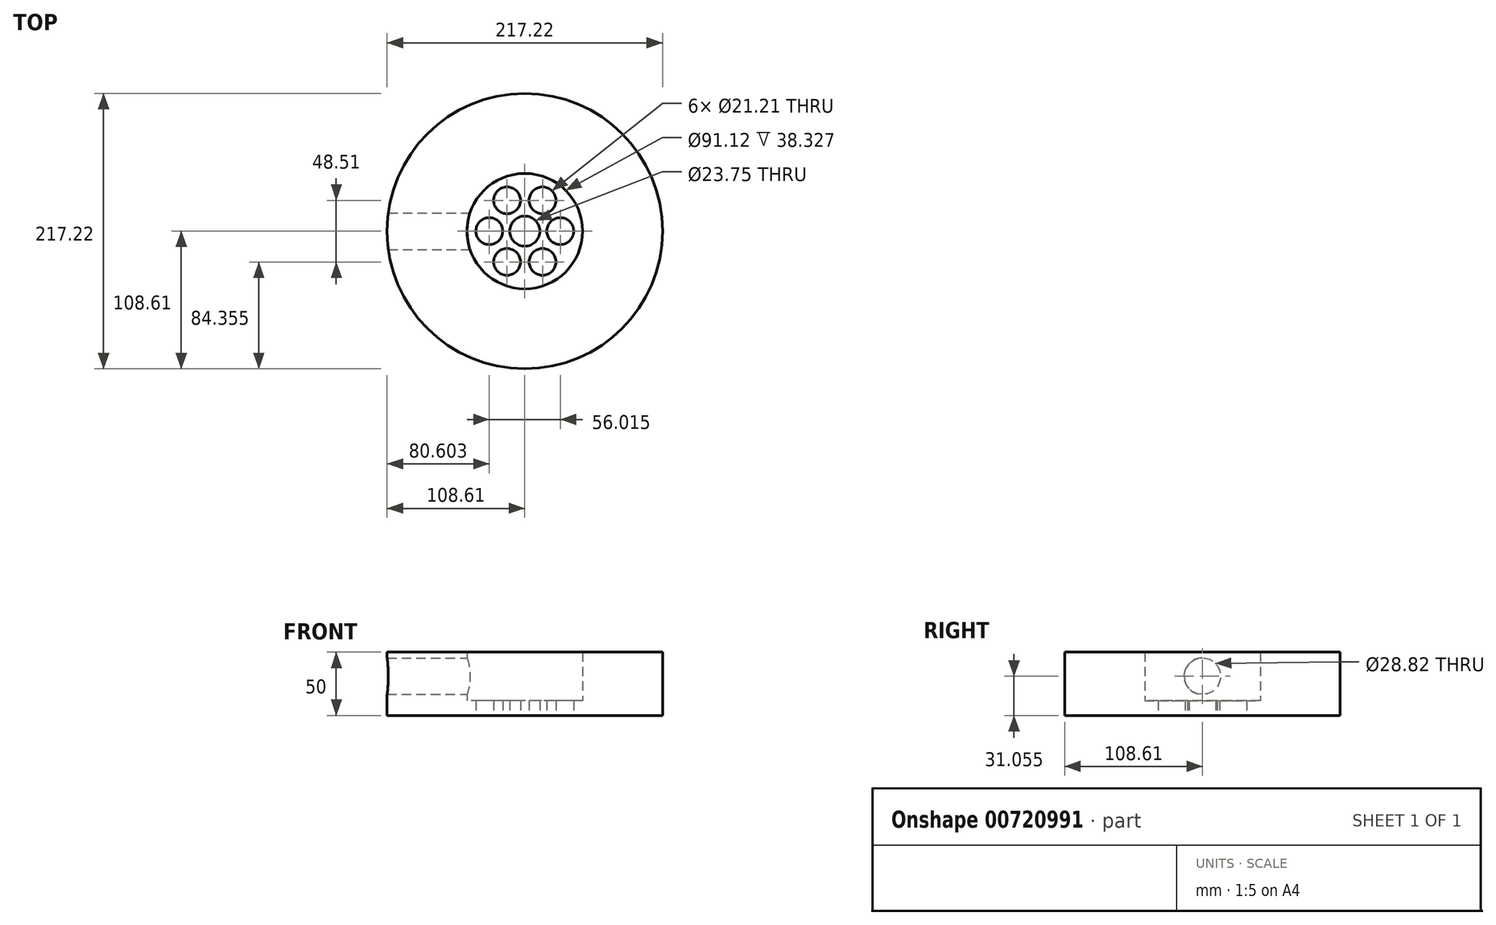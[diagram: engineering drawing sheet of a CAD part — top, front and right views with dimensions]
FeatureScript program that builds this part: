
annotation { "Feature Type Name" : "Feature", "Feature Type Description" : "" }
export const myFeature = defineFeature(function(context is Context, id is Id, definition is map)
    precondition{}
    {
        {
            var Q0;
            Q0=qCreatedBy(makeId("Top.planeOp"),FACE);
            var sketch = newSketch(context, id + "F0", { "sketchPlane" : qUnion([Q0])});
            skCircle(sketch, "E0", {"center": v(0, 0) * mm, "radius": 108.61 * mm});
            skCircle(sketch, "E1", {"center": v(0, 0) * mm, "radius": 45.56 * mm});
            skCircle(sketch, "E2", {"center": v(0, 0) * mm, "radius": 11.88 * mm});
            skCircle(sketch, "E3", {"center": v(-28, 0) * mm, "radius": 10.6 * mm});
            skCircle(sketch, "E4.1.0", {"center": v(-14, -24.25) * mm, "radius": 10.6 * mm});
            skCircle(sketch, "E4.2.0", {"center": v(14, -24.25) * mm, "radius": 10.6 * mm});
            skCircle(sketch, "E4.3.0", {"center": v(28, 0) * mm, "radius": 10.6 * mm});
            skCircle(sketch, "E4.4.0", {"center": v(14, 24.25) * mm, "radius": 10.6 * mm});
            skCircle(sketch, "E4.5.0", {"center": v(-14, 24.25) * mm, "radius": 10.6 * mm});
            skSolve(sketch);
        }
        {
            var Q0;
            Q0 = qSketchRegion(id + "F0", true);
            extrude(context, id + "F1", {"entities" : qUnion([Q0]), "depth" : 50 * mm, "offsetDistance" : 25 * mm});
        }
        {
            var Q0;
            Q0=makeQuery(id+"F0.imprint","IMPRINT",FACE,{"disambiguationData":[TD([[makeQuery(id+"F0.imprint","IMPRINT",EDGE,{"derivedFrom":sQuery(id+"F0.wireOp",EDGE,"E1")}),1.0]])]});
            extrude(context, id + "F2", {"entities" : qUnion([Q0]), "operationType" : NewBodyOperationType.ADD, "depth" : 11.67 * mm, "offsetDistance" : 25 * mm});
        }
        {
            var Q0;
            Q0=qCreatedBy(makeId("Right.planeOp"),FACE);
            var sketch = newSketch(context, id + "F3", { "sketchPlane" : qUnion([Q0])});
            skCircle(sketch, "E5", {"center": v(0, 31.06) * mm, "radius": 14.41 * mm});
            skSolve(sketch);
        }
        {
            var Q0;
            Q0 = qSketchRegion(id + "F3", true);
            var Q1;
            Q1=makeQuery(id+"F1.opExtrude","SWEPT_FACE",FACE,{"disambiguationData":[OSD([sQuery(id+"F0.wireOp",EDGE,"E0")])]});
            extrude(context, id + "F4", {"entities" : qUnion([Q0]), "operationType" : NewBodyOperationType.REMOVE, "endBound" : BoundingType.UP_TO_SURFACE, "oppositeDirection" : true, "depth" : 25 * mm, "endBoundEntityFace" : qUnion([Q1]), "offsetDistance" : 25 * mm});
        }
        {
            var Q0;
            Q0=qCreatedBy(makeId("Front.planeOp"),FACE);
            var sketch = newSketch(context, id + "F5", { "sketchPlane" : qUnion([Q0])});
            skFitSpline(sketch, "E6", {"points": [v(17.4, 11.67) * mm, v(45.56, 45.47) * mm], "startDerivative": vector(-8.12, 73.98) * mm, "endDerivative": vector(61.97, -2.03) * mm});
            skFitSpline(sketch, "E7", {"points": [v(38.61, 11.67) * mm, v(45.56, 16.64) * mm], "startDerivative": vector(0.18, 10.79) * mm, "endDerivative": vector(12.4, -1.23) * mm});
            skFitSpline(sketch, "E8.0", {"points": [v(45.56, 16.64) * mm, v(45.56, 16.65) * mm, v(45.51, 16.78) * mm, v(45.37, 17.25) * mm, v(45.23, 17.73) * mm, v(45.05, 18.34) * mm, v(44.85, 19.07) * mm, v(44.63, 19.91) * mm, v(44.4, 20.85) * mm, v(44.18, 21.9) * mm, v(43.88, 23.41) * mm, v(43.65, 24.85) * mm, v(43.5, 26.18) * mm, v(43.4, 27.08) * mm, v(43.3, 28.23) * mm, v(43.25, 29.4) * mm, v(43.22, 30.34) * mm, v(43.22, 31.06) * mm, v(43.22, 31.78) * mm, v(43.25, 32.72) * mm, v(43.3, 33.89) * mm, v(43.4, 35.03) * mm, v(43.5, 35.94) * mm, v(43.65, 37.26) * mm, v(43.88, 38.7) * mm, v(44.18, 40.22) * mm, v(44.4, 41.26) * mm, v(44.63, 42.2) * mm, v(44.85, 43.04) * mm, v(45.05, 43.78) * mm, v(45.23, 44.38) * mm, v(45.37, 44.86) * mm, v(45.51, 45.33) * mm, v(45.56, 45.46) * mm, v(45.56, 45.47) * mm]});
            skLineSegment(sketch, "E9.0", {"start": v(17.4, 11.67) * mm, "end": v(38.61, 11.67) * mm});
            skLineSegment(sketch, "E10", {"start": v(45.56, 16.64) * mm, "end": v(45.56, 45.47) * mm});
            skSolve(sketch);
        }
    });
